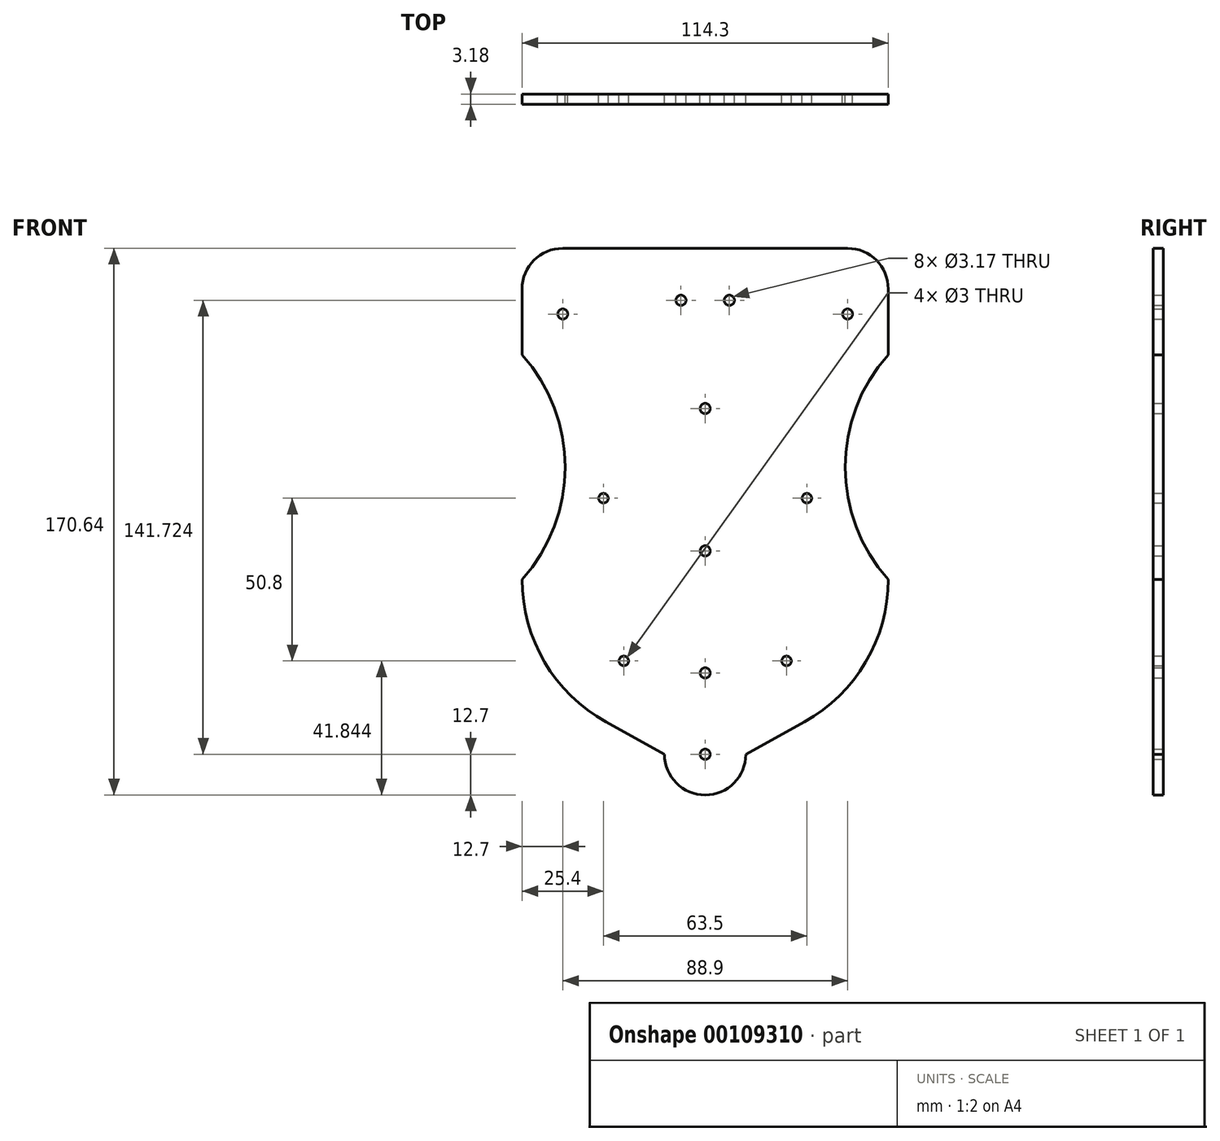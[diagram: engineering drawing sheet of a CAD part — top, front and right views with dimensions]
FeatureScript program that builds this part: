
annotation { "Feature Type Name" : "Feature", "Feature Type Description" : "" }
export const myFeature = defineFeature(function(context is Context, id is Id, definition is map)
    precondition{}
    {
        {
            var Q0;
            Q0=qCreatedBy(makeId("Front.planeOp"),FACE);
            var sketch = newSketch(context, id + "F0", { "sketchPlane" : qUnion([Q0])});
            skCircle(sketch, "E0", {"center": v(0, 0) * mm, "radius": 12.7 * mm});
            skLineSegment(sketch, "E1", {"start": v(-12.7, 0) * mm, "end": v(-30.94, 10.1) * mm});
            skLineSegment(sketch, "E2", {"start": v(-57.15, 54.54) * mm, "end": v(-57.15, 145.24) * mm});
            skLineSegment(sketch, "E3", {"start": v(-12.7, 0) * mm, "end": v(12.7, 0) * mm, "construction": true});
            skLineSegment(sketch, "E4", {"start": v(0, 0) * mm, "end": v(0, 253.2) * mm, "construction": true});
            skLineSegment(sketch, "E5.MirrorCS", {"start": v(12.7, 0) * mm, "end": v(30.94, 10.1) * mm});
            skLineSegment(sketch, "E6.MirrorCS", {"start": v(57.15, 54.54) * mm, "end": v(57.15, 145.24) * mm});
            skCircle(sketch, "E7", {"center": v(0, 63.5) * mm, "radius": 25.4 * mm, "construction": true});
            skCircle(sketch, "E8", {"center": v(0, 63.5) * mm, "radius": 19.05 * mm, "construction": true});
            skCircle(sketch, "E9", {"center": v(0, 107.95) * mm, "radius": 25.4 * mm, "construction": true});
            skCircle(sketch, "E10", {"center": v(-44.45, 137.43) * mm, "radius": 27.94 * mm, "construction": true});
            skCircle(sketch, "E11", {"center": v(0, 0) * mm, "radius": 76.2 * mm, "construction": true});
            skCircle(sketch, "E12", {"center": v(0, 25.4) * mm, "radius": 12.7 * mm, "construction": true});
            skCircle(sketch, "E13", {"center": v(-44.45, 137.43) * mm, "radius": 41.28 * mm, "construction": true});
            skLineSegment(sketch, "E14", {"start": v(-44.45, 137.43) * mm, "end": v(44.45, 137.43) * mm, "construction": true});
            skCircle(sketch, "E15", {"center": v(44.45, 137.43) * mm, "radius": 41.28 * mm, "construction": true});
            skCircle(sketch, "E16", {"center": v(-44.45, 137.43) * mm, "radius": 1.59 * mm});
            skCircle(sketch, "E17", {"center": v(44.45, 137.43) * mm, "radius": 1.59 * mm});
            skCircle(sketch, "E18", {"center": v(0, 107.95) * mm, "radius": 1.59 * mm});
            skCircle(sketch, "E19", {"center": v(0, 63.5) * mm, "radius": 1.59 * mm});
            skCircle(sketch, "E20", {"center": v(0, 25.4) * mm, "radius": 1.59 * mm});
            skCircle(sketch, "E21", {"center": v(0, 0) * mm, "radius": 1.59 * mm});
            skPoint(sketch, "E22.visualSharp", {"position": v(57.15, 24.6) * mm});
            skArc(sketch, "E22.filletArc", {"start": v(30.94, 10.1) * mm, "mid": v(50.11, 28.74) * mm, "end": v(57.15, 54.54) * mm});
            skPoint(sketch, "E23.visualSharp", {"position": v(-57.15, 24.6) * mm});
            skArc(sketch, "E23.filletArc", {"start": v(-57.15, 54.54) * mm, "mid": v(-50.11, 28.74) * mm, "end": v(-30.94, 10.1) * mm});
            skLineSegment(sketch, "E24", {"start": v(-57.15, 54.54) * mm, "end": v(-31.75, 54.54) * mm, "construction": true});
            skLineSegment(sketch, "E25", {"start": v(-31.75, 54.54) * mm, "end": v(-31.75, 29.14) * mm, "construction": true});
            skLineSegment(sketch, "E26", {"start": v(-31.75, 29.14) * mm, "end": v(-19.05, 29.14) * mm, "construction": true});
            skLineSegment(sketch, "E27", {"start": v(-19.05, 29.14) * mm, "end": v(-19.05, 3.51) * mm, "construction": true});
            skCircle(sketch, "E28", {"center": v(-25.4, 29.14) * mm, "radius": 1.5 * mm});
            skCircle(sketch, "E29.MirrorC", {"center": v(25.4, 29.14) * mm, "radius": 1.5 * mm});
            skPoint(sketch, "E30.visualSharp", {"position": v(-57.15, 202.4) * mm});
            skPoint(sketch, "E31.visualSharp", {"position": v(57.15, 202.4) * mm});
            skCircle(sketch, "E32", {"center": v(-7.55, 141.72) * mm, "radius": 1.59 * mm});
            skCircle(sketch, "E33.MirrorC", {"center": v(7.55, 141.72) * mm, "radius": 1.59 * mm});
            skLineSegment(sketch, "E34", {"start": v(-44.45, 157.94) * mm, "end": v(44.45, 157.94) * mm});
            skCircle(sketch, "E35", {"center": v(-31.75, 79.94) * mm, "radius": 1.5 * mm});
            skCircle(sketch, "E36.MirrorC", {"center": v(31.75, 79.94) * mm, "radius": 1.5 * mm});
            skLineSegment(sketch, "E37", {"start": v(-25.4, 29.14) * mm, "end": v(25.4, 29.14) * mm, "construction": true});
            skPoint(sketch, "E38.visualSharp", {"position": v(-57.15, 157.94) * mm});
            skArc(sketch, "E38.filletArc", {"start": v(-44.45, 157.94) * mm, "mid": v(-53.43, 154.22) * mm, "end": v(-57.15, 145.24) * mm});
            skPoint(sketch, "E39.visualSharp", {"position": v(57.15, 157.94) * mm});
            skArc(sketch, "E39.filletArc", {"start": v(57.15, 145.24) * mm, "mid": v(53.43, 154.22) * mm, "end": v(44.45, 157.94) * mm});
            skArc(sketch, "E40", {"start": v(-57.15, 54.54) * mm, "mid": v(-43.73, 89.64) * mm, "end": v(-57.15, 124.73) * mm});
            skArc(sketch, "E41.MirrorCS", {"start": v(57.15, 54.54) * mm, "mid": v(43.73, 89.64) * mm, "end": v(57.15, 124.73) * mm});
            skSolve(sketch);
        }
        {
            var Q0;
            Q0=makeQuery(id+"F0.imprint","IMPRINT",FACE,{"disambiguationData":[TD([[makeQuery(id+"F0.imprint","IMPRINT",EDGE,{"derivedFrom":sQuery(id+"F0.wireOp",EDGE,"E21")}),-1.0]])]});
            var Q1;
            {var subQ5=sQuery(id+"F0.wireOp",EDGE,"E1");Q1=makeQuery(id+"F0.imprint","IMPRINT",FACE,{"disambiguationData":[TD([[makeQuery(id+"F0.imprint","IMPRINT",EDGE,{"derivedFrom":subQ5}),-1.0]])]});}
            extrude(context, id + "F1", {"entities" : qUnion([Q0, Q1]), "depth" : 3.17 * mm});
        }
    });
